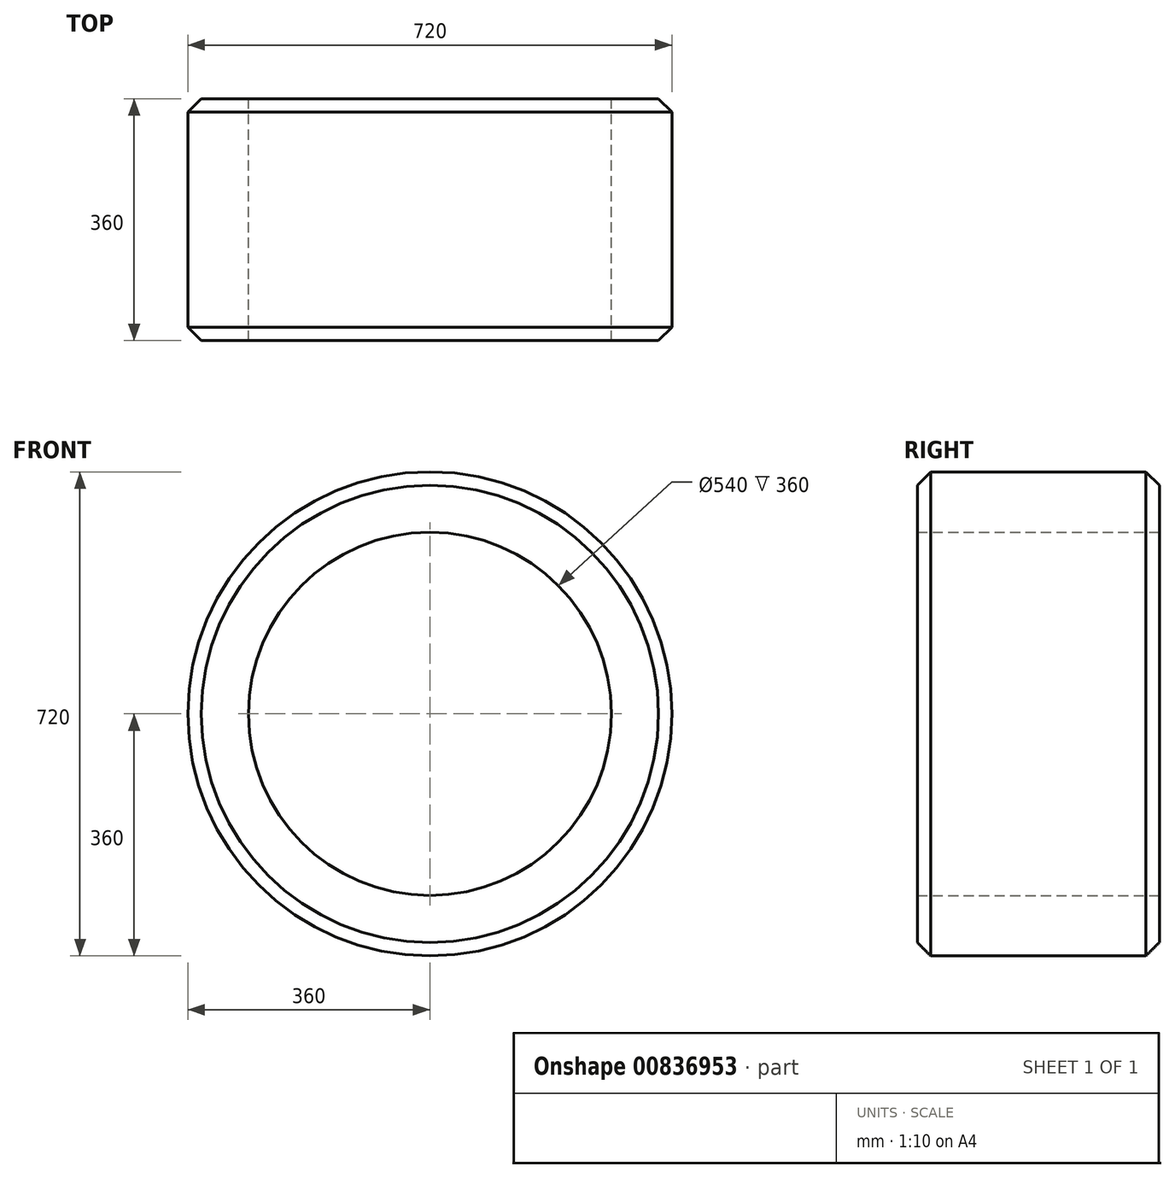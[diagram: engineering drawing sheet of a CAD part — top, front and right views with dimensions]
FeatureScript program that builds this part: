
annotation { "Feature Type Name" : "Feature", "Feature Type Description" : "" }
export const myFeature = defineFeature(function(context is Context, id is Id, definition is map)
    precondition{}
    {
        {
            var Q0;
            Q0=qCreatedBy(makeId("Front.planeOp"),FACE);
            var sketch = newSketch(context, id + "F0", { "sketchPlane" : qUnion([Q0])});
            skCircle(sketch, "E0", {"center": v(0, 0) * mm, "radius": 270 * mm});
            skCircle(sketch, "E1", {"center": v(0, 0) * mm, "radius": 360 * mm});
            skSolve(sketch);
        }
        {
            var Q0;
            Q0=makeQuery(id+"F0.imprint","IMPRINT",FACE,{"disambiguationData":[TD([[makeQuery(id+"F0.imprint","IMPRINT",EDGE,{"derivedFrom":sQuery(id+"F0.wireOp",EDGE,"E0")}),-1.0]])]});
            extrude(context, id + "F1", {"entities" : qUnion([Q0]), "endBound" : BoundingType.SYMMETRIC, "depth" : 360 * mm, "offsetDistance" : 25 * mm});
        }
        {
            var Q0;
            Q0=makeQuery(id+"F1.opExtrude","CAP_EDGE",EDGE,{"disambiguationData":[OSD([sQuery(id+"F0.wireOp",EDGE,"E1")])],"isStart":false});
            chamfer(context, id + "F2", {"entities" : qUnion([Q0]), "width" : 20 * mm, "tangentPropagation" : true});
        }
        {
            var Q0;
            Q0=makeQuery(id+"F1.opExtrude","CAP_EDGE",EDGE,{"disambiguationData":[OSD([sQuery(id+"F0.wireOp",EDGE,"E1")])],"isStart":true});
            chamfer(context, id + "F3", {"entities" : qUnion([Q0]), "width" : 20 * mm, "tangentPropagation" : true});
        }
    });
